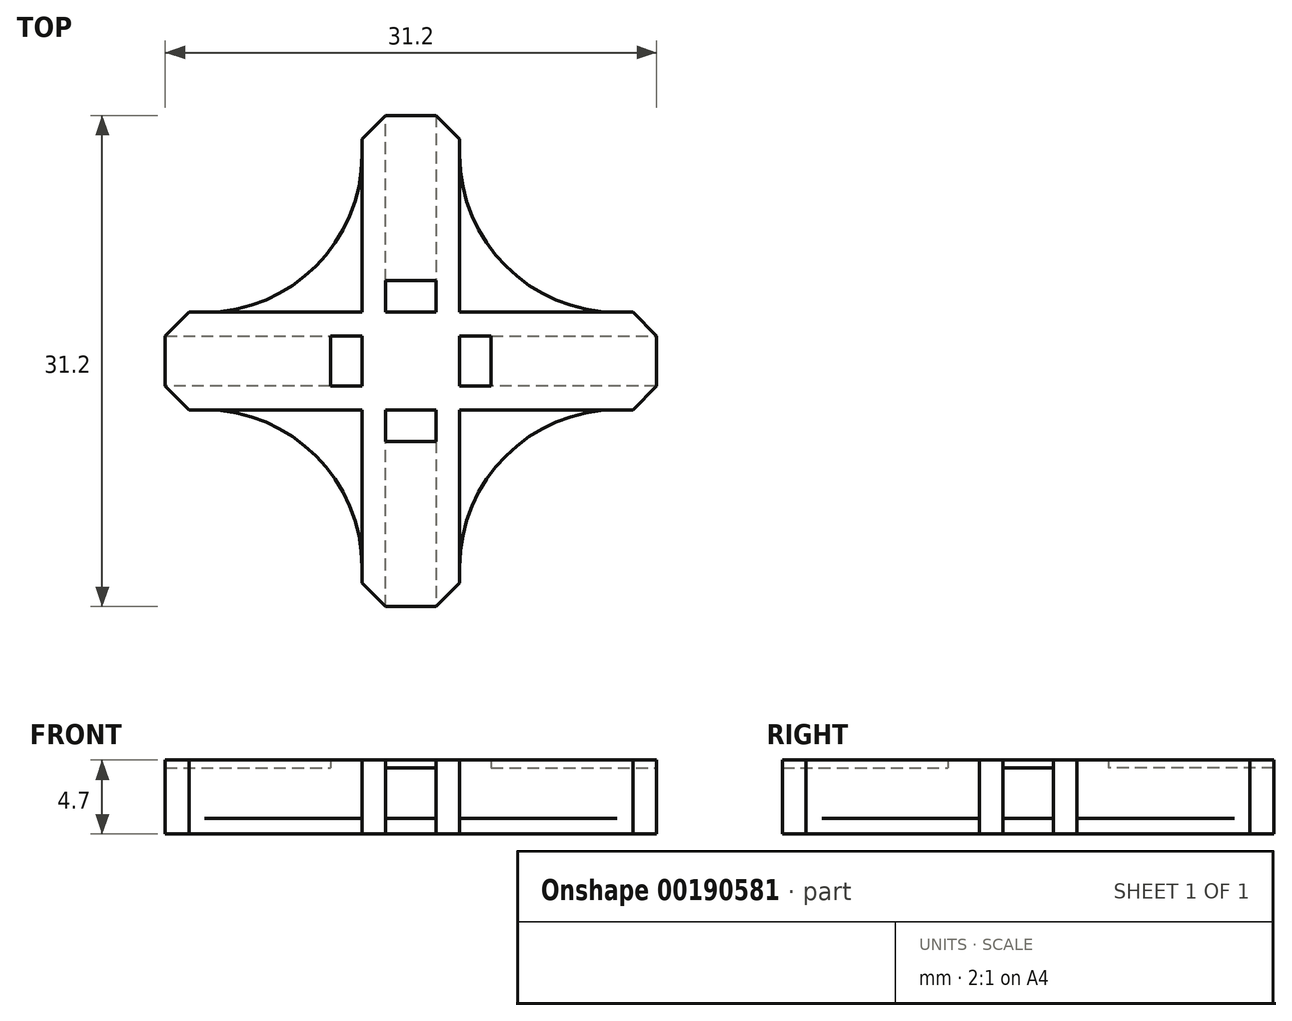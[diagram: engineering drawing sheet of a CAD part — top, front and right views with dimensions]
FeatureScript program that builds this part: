
annotation { "Feature Type Name" : "Feature", "Feature Type Description" : "" }
export const myFeature = defineFeature(function(context is Context, id is Id, definition is map)
    precondition{}
    {
        {
            var Q0;
            Q0=qCreatedBy(makeId("Top.planeOp"),FACE);
            var sketch = newSketch(context, id + "F0", { "sketchPlane" : qUnion([Q0])});
            skLineSegment(sketch, "E0", {"start": v(1.6, 15.6) * mm, "end": v(1.6, 1.6) * mm});
            skLineSegment(sketch, "E1", {"start": v(1.6, 1.6) * mm, "end": v(15.6, 1.6) * mm});
            skLineSegment(sketch, "E2.0", {"start": v(3.1, 3.1) * mm, "end": v(14.1, 3.1) * mm});
            skLineSegment(sketch, "E2.1", {"start": v(3.1, 14.1) * mm, "end": v(3.1, 3.1) * mm});
            skPoint(sketch, "E3.center", {"position": v(0, 0) * mm});
            skLineSegment(sketch, "E4", {"start": v(0, 17.2) * mm, "end": v(0, 0) * mm, "construction": true});
            skLineSegment(sketch, "E5", {"start": v(0, 0) * mm, "end": v(17.2, 0) * mm, "construction": true});
            skLineSegment(sketch, "E6", {"start": v(0, 17.2) * mm, "end": v(17.2, 0) * mm, "construction": true});
            skLineSegment(sketch, "E7", {"start": v(1.6, 15.6) * mm, "end": v(0, 15.6) * mm});
            skLineSegment(sketch, "E8", {"start": v(15.6, 1.6) * mm, "end": v(15.6, 0) * mm});
            skLineSegment(sketch, "E9", {"start": v(15.6, 1.6) * mm, "end": v(14.1, 3.1) * mm});
            skLineSegment(sketch, "E10", {"start": v(3.1, 14.1) * mm, "end": v(1.6, 15.6) * mm});
            skLineSegment(sketch, "E11", {"start": v(0, 15.6) * mm, "end": v(0, 0) * mm});
            skLineSegment(sketch, "E12", {"start": v(0, 0) * mm, "end": v(15.6, 0) * mm});
            skLineSegment(sketch, "E13", {"start": v(1.6, 3.1) * mm, "end": v(0, 3.1) * mm});
            skLineSegment(sketch, "E14", {"start": v(3.1, 1.6) * mm, "end": v(3.1, 0) * mm});
            skSolve(sketch);
        }
        {
            var Q0;
            Q0=makeQuery(id+"F0.imprint","IMPRINT",FACE,{"disambiguationData":[TD([[makeQuery(id+"F0.imprint","IMPRINT",EDGE,{"derivedFrom":sQuery(id+"F0.wireOp",EDGE,"E0")}),1.0]])]});
            var Q1;
            Q1=makeQuery(id+"F0.imprint","IMPRINT",FACE,{"disambiguationData":[TD([[makeQuery(id+"F0.imprint","IMPRINT",EDGE,{"derivedFrom":sQuery(id+"F0.wireOp",EDGE,"E0")}),-1.0]])]});
            var Q2;
            Q2=makeQuery(id+"F0.imprint","IMPRINT",FACE,{"disambiguationData":[TD([[makeQuery(id+"F0.imprint","IMPRINT",EDGE,{"derivedFrom":sQuery(id+"F0.wireOp",EDGE,"E1")}),-1.0]])]});
            var Q3;
            {var subQ4=sQuery(id+"F0.wireOp",EDGE,"nSCJROIS-KGDO-uwYD-OSe6-LGbfKK9FbWBD");Q3=makeQuery(id+"F0.imprint","IMPRINT",FACE,{"disambiguationData":[TD([[makeQuery(id+"F0.imprint","IMPRINT",EDGE,{"derivedFrom":subQ4}),-1.0]])]});}
            var Q4;
            {var subQ4=sQuery(id+"F0.wireOp",EDGE,"E13");Q4=makeQuery(id+"F0.imprint","IMPRINT",FACE,{"disambiguationData":[TD([[makeQuery(id+"F0.imprint","IMPRINT",EDGE,{"derivedFrom":subQ4}),1.0]])]});}
            extrude(context, id + "F1", {"entities" : qUnion([Q0, Q1, Q2, Q3, Q4]), "oppositeDirection" : true, "depth" : 1 * mm});
        }
        {
            var Q0;
            Q0=makeQuery(id+"F1.opExtrude","SWEPT_EDGE",EDGE,{"disambiguationData":[OSD([sQuery(id+"F0.wireOp",EDGE,"E2.0"),sQuery(id+"F0.wireOp",EDGE,"E2.1")])]});
            fillet(context, id + "F2", {"entities" : qUnion([Q0]), "radius" : 10 * mm, "tangentPropagation" : true, "allowEdgeOverflow" : false});
        }
        {
            var Q0;
            Q0=makeQuery(id+"F0.imprint","IMPRINT",FACE,{"disambiguationData":[TD([[makeQuery(id+"F0.imprint","IMPRINT",EDGE,{"derivedFrom":sQuery(id+"F0.wireOp",EDGE,"E0")}),1.0]])]});
            var Q1;
            {var subQ4=sQuery(id+"F0.wireOp",EDGE,"nSCJROIS-KGDO-uwYD-OSe6-LGbfKK9FbWBD");Q1=makeQuery(id+"F0.imprint","IMPRINT",FACE,{"disambiguationData":[TD([[makeQuery(id+"F0.imprint","IMPRINT",EDGE,{"derivedFrom":subQ4}),-1.0]])]});}
            var Q2;
            {var subQ4=sQuery(id+"F0.wireOp",EDGE,"E13");Q2=makeQuery(id+"F0.imprint","IMPRINT",FACE,{"disambiguationData":[TD([[makeQuery(id+"F0.imprint","IMPRINT",EDGE,{"derivedFrom":subQ4}),1.0]])]});}
            extrude(context, id + "F3", {"entities" : qUnion([Q0, Q1, Q2]), "operationType" : NewBodyOperationType.ADD, "depth" : 3.2 * mm});
        }
        {
            var Q0;
            Q0=makeQuery(id+"F1.opExtrude","SWEPT_BODY",BODY,{"disambiguationData":[OSD([sQuery(id+"F0.wireOp",EDGE,"E2.0"),sQuery(id+"F0.wireOp",EDGE,"E2.1"),sQuery(id+"F0.wireOp",EDGE,"E7"),sQuery(id+"F0.wireOp",EDGE,"E8"),sQuery(id+"F0.wireOp",EDGE,"E9"),sQuery(id+"F0.wireOp",EDGE,"E10"),sQuery(id+"F0.wireOp",EDGE,"E11"),sQuery(id+"F0.wireOp",EDGE,"E12")])]});
            var Q1;
            Q1=makeQuery(id+"F1.opExtrude","SWEPT_EDGE",EDGE,{"disambiguationData":[OSD([sQuery(id+"F0.wireOp",EDGE,"E11"),sQuery(id+"F0.wireOp",EDGE,"E12")])]});
            circularPattern(context, id + "F4", {"operationType" : NewBodyOperationType.ADD, "entities" : qUnion([Q0]), "axis" : qUnion([Q1]), "angle" : 360 * degree, "instanceCount" : 4, "equalSpace" : true});
        }
        {
            var Q0;
            {var subQ0=makeQuery(id+"F3.opExtrude","CAP_FACE",FACE,{"disambiguationData":[OSD([sQuery(id+"F0.wireOp",EDGE,"E0"),sQuery(id+"F0.wireOp",EDGE,"E1"),sQuery(id+"F0.wireOp",EDGE,"E2.0"),sQuery(id+"F0.wireOp",EDGE,"E2.1"),sQuery(id+"F0.wireOp",EDGE,"E9"),sQuery(id+"F0.wireOp",EDGE,"E10"),sQuery(id+"F0.wireOp",EDGE,"E11"),sQuery(id+"F0.wireOp",EDGE,"E12"),sQuery(id+"F0.wireOp",EDGE,"E13"),sQuery(id+"F0.wireOp",EDGE,"E14")])],"isStart":false});Q0=makeQuery(id+"F4.boolean.opBoolean","MERGE",FACE,{"derivedFrom":[subQ0,makeQuery(id+"F4.opPattern","COPY",FACE,{"derivedFrom":subQ0,"instanceName":"1"}),makeQuery(id+"F4.opPattern","COPY",FACE,{"derivedFrom":subQ0,"instanceName":"2"}),makeQuery(id+"F4.opPattern","COPY",FACE,{"derivedFrom":subQ0,"instanceName":"3"})]});}
            var sketch = newSketch(context, id + "F5", { "sketchPlane" : qUnion([Q0])});
            skLineSegment(sketch, "E15.0", {"start": v(-1.6, 15.6) * mm, "end": v(-3.1, 14.1) * mm});
            skLineSegment(sketch, "E15.1", {"start": v(-3.1, 3.1) * mm, "end": v(-3.1, 14.1) * mm});
            skLineSegment(sketch, "E15.2", {"start": v(1.6, 15.6) * mm, "end": v(-1.6, 15.6) * mm});
            skLineSegment(sketch, "E15.3", {"start": v(3.1, 14.1) * mm, "end": v(1.6, 15.6) * mm});
            skLineSegment(sketch, "E15.4", {"start": v(3.1, 14.1) * mm, "end": v(3.1, 3.1) * mm});
            skLineSegment(sketch, "E16", {"start": v(-3.1, 3.1) * mm, "end": v(0, 0) * mm});
            skLineSegment(sketch, "E17", {"start": v(0, 0) * mm, "end": v(3.1, 3.1) * mm});
            skLineSegment(sketch, "E18.bottom", {"start": v(-1.6, 3.1) * mm, "end": v(1.6, 3.1) * mm});
            skLineSegment(sketch, "E18.top", {"start": v(-1.6, 5.1) * mm, "end": v(1.6, 5.1) * mm});
            skLineSegment(sketch, "E18.left", {"start": v(-1.6, 3.1) * mm, "end": v(-1.6, 5.1) * mm});
            skLineSegment(sketch, "E18.right", {"start": v(1.6, 3.1) * mm, "end": v(1.6, 5.1) * mm});
            skSolve(sketch);
        }
        {
            var Q0;
            Q0 = qSketchRegion(id + "F5", true);
            extrude(context, id + "F6", {"entities" : qUnion([Q0]), "depth" : .5 * mm});
        }
        {
            var Q0;
            Q0=makeQuery(id+"F6.opExtrude","SWEPT_BODY",BODY,{"disambiguationData":[OSD([sQuery(id+"F5.wireOp",EDGE,"E15.0"),sQuery(id+"F5.wireOp",EDGE,"E15.1"),sQuery(id+"F5.wireOp",EDGE,"E15.2"),sQuery(id+"F5.wireOp",EDGE,"E15.3"),sQuery(id+"F5.wireOp",EDGE,"E15.4"),sQuery(id+"F5.wireOp",EDGE,"E16"),sQuery(id+"F5.wireOp",EDGE,"E17"),sQuery(id+"F5.wireOp",EDGE,"E18.bottom"),sQuery(id+"F5.wireOp",EDGE,"E18.top"),sQuery(id+"F5.wireOp",EDGE,"E18.left"),sQuery(id+"F5.wireOp",EDGE,"E18.right")])]});
            var Q1;
            Q1=makeQuery(id+"F6.opExtrude","SWEPT_EDGE",EDGE,{"disambiguationData":[OSD([sQuery(id+"F5.wireOp",EDGE,"E16"),sQuery(id+"F5.wireOp",EDGE,"E17")])]});
            circularPattern(context, id + "F7", {"operationType" : NewBodyOperationType.ADD, "entities" : qUnion([Q0]), "axis" : qUnion([Q1]), "angle" : 360 * degree, "instanceCount" : 4, "equalSpace" : true});
        }
    });
